# Revit family: Faucet-Kitchen-KOHLER-Purist-K-7509
name_source: partatom
category: Plumbing Fixtures
revit_build: Autodesk Revit 2015 (Build: 20140606_1530(x64)
units: mm (PartAtom-declared; Revit-internal decimal feet)

## types (4) — shared parameters
ADA Compliant = Yes
Assembly Code = D2010
CW Connection = Yes
Cold Water Inlet = Cold Water Inlet
Date Modified = 02/12/2019
Default Elevation = 36"
Description = single-Hole Kitchen Sink Faucet With 6inch Spout
Drain Included = No
Faucet Hole Spacing = 0"
Flow Rate = 2 GPM
HW Connection = Yes
Handle Clearance = 3"
Height = 9 7/8"
Hot Water Inlet = Hot Water Inlet
Length = 6"
Manufacturer = KOHLER Co.
MasterFormat 1995 = 15410
MasterFormat 2004 = 22.41.39
Material = Premium metal construction
Pressure = 60.00 psi
Product Documentation Link = https://www.us.kohler.com
Product Name = Purist
Product Page URL = http://www.us.kohler.com
Spout Reach = 6"
URL = https://www.us.kohler.com
Vent Connection = No
Waste Connection = No
Waste Water Outlet = Waste Water Outlet
WaterSense Certified = No
Width = 2"

## per-type parameters (varying)
| type | Finish | Model | Type |
| CP Polished Chrome | Kohler-Metal-CP-Polished_Chrome | K-7509-CP | 1 |
| SN Vibrant Polished Nickel | Kohler-Metal-SN-Vibrant_Polished_Nickel | K-7509-SN | 2 |
| VS Vibrant Stainless | Kohler-Metal-VS-Vibrant_Stainless | K-7509-VS | 3 |
| BL Matte Black | Kohler-Metal-BL-Matte_Black | K-7509-BL | 4 |

## geometry (parser evidence)
native form markers: Sweep x5
no freeform markers — native parametric forms only
